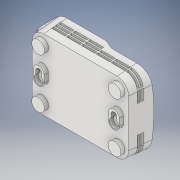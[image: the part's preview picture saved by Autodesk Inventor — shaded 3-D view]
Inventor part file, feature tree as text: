
AUTODESK INVENTOR PART (.ipt)
format: ipt  version: 2019 (Build 230136000, 136)  size: 717,312 bytes
history: native  units: in
note: dims shown in document units (in); Inventor stores cm internally (conversion verified against a paired STEP export)
features: projected_geometry x18, sketch x15, extrude x14, plane x6, fillet x1, pattern_linear x1
ambient origin geometry x8: Origin, YZ Plane, XZ Plane, XY Plane, X Axis, Y Axis, Z Axis, Center Point
bodies: Solid1 (feature_tree)
feature tree (55):
  extrude  "Extrusion1"  Depth=2.755in
  plane  "Work Plane2"
  extrude  "Extrusion2"  Depth=0.5in
  fillet  "Fillet1"  Radius=0.36in
  plane  "Work Plane3"
  extrude  "Extrusion3"  Depth=0.72in
  extrude  "Extrusion4"  Depth=0.5in
  extrude  "Extrusion5"  Depth=0.125in
  extrude  "Extrusion6"  Depth=0.04in
  plane  "Work Plane4"
  extrude  "Extrusion7"  Depth=0.13in
  plane  "Work Plane5"
  sketch  "Sketch11"  dims[d17=1.855in d18=0.0in d19=1.855in d20=0.0in]
  extrude  "Extrusion8"  Depth=1.855in TaperAngle=0.0deg
  plane  "Work Plane6"
  extrude  "Extrusion9"  Depth=1.855in TaperAngle=0.0deg
  extrude  "Extrusion10"  Depth=0.5in
  pattern_linear  "Rectangular Pattern1"  Count1=3 Spacing1=0.125in
  extrude  "Extrusion11"  Depth=0.295in
  extrude  "Extrusion12"  Depth=0.5in TaperAngle=0.0deg
  plane  "Work Plane7"
  extrude  "Extrusion13"  Depth=0.5425in TaperAngle=0.0deg
  extrude  "Extrusion14"  Depth=0.001in
  sketch  "Sketch1"  dims[d0=3.71in d1=2.755in]
  sketch  "Sketch4"  dims[d2=0.5in d3=0.855in d4=-0.0344in d5=0.36in]
  sketch  "Sketch5"  dims[d6=0.72in d7=0.72in]
  sketch  "Sketch6"  dims[d8=1.855in d9=0.0in d10=0.5in]
  projected_geometry  "Projected Loop1"
  sketch  "Sketch7"  dims[d11=-1.86in d12=0.125in]
  projected_geometry  "Projected Loop2"
  sketch  "Sketch8"  dims[d13=0.04in d14=0.65in]
  projected_geometry  "Projected Loop3"
  sketch  "Sketch9"  dims[d15=0.13in d16=0.13in]
  sketch  "Sketch12"  dims[d21=1.855in d22=0.0in d23=1.855in d24=0.0in]
  projected_geometry  "Projected Loop4"
  projected_geometry  "Projected Loop5"
  projected_geometry  "Projected Loop6"
  projected_geometry  "Projected Loop7"
  projected_geometry  "Projected Loop8"
  projected_geometry  "Projected Loop9"
  projected_geometry  "Projected Loop10"
  projected_geometry  "Projected Loop11"
  projected_geometry  "Projected Loop12"
  projected_geometry  "Projected Loop13"
  projected_geometry  "Projected Loop14"
  projected_geometry  "Projected Loop15"
  projected_geometry  "Projected Loop16"
  projected_geometry  "Projected Loop17"
  projected_geometry  "Projected Loop18"
  sketch  "Sketch13"  dims[d25=1.5in d26=0.5in]
  sketch  "Sketch14"  dims[d27=0.075in d28=1.1811in d30=0.125in d31=1.1811in d33=0.55in]
  sketch  "Sketch15"  dims[d36=1.5748in d38=0.55in d39=0.7874in d41=0.125in d44=0.295in]
  sketch  "Sketch16"  dims[d45=0.5in d46=0.5425in d47=0.0in]
  sketch  "Sketch17"  dims[d48=-1.375in d49=0.5425in d50=0.0in]
  sketch  "Sketch18"  dims[d51=1.875in d52=0.4in d53=0.4in d54=0.05in d55=0.05in d56=0.1675in d57=0.0in d59=0.436in d60=0.272in d61=0.325in d62=0.472in d63=0.07in d64=0.1675in d65=0.0in d66=0.03in d67=0.03in d68=0.7874in d70=0.6in d71=0.35in d72=0.45in d73=0.02in d74=0.0in d75=0.145in d76=0.0in d77=0.15in d78=0.26in d79=0.335in d80=0.216in d81=0.145in d82=0.0in d83=0.472in d84=0.001in d85=0.0in]
